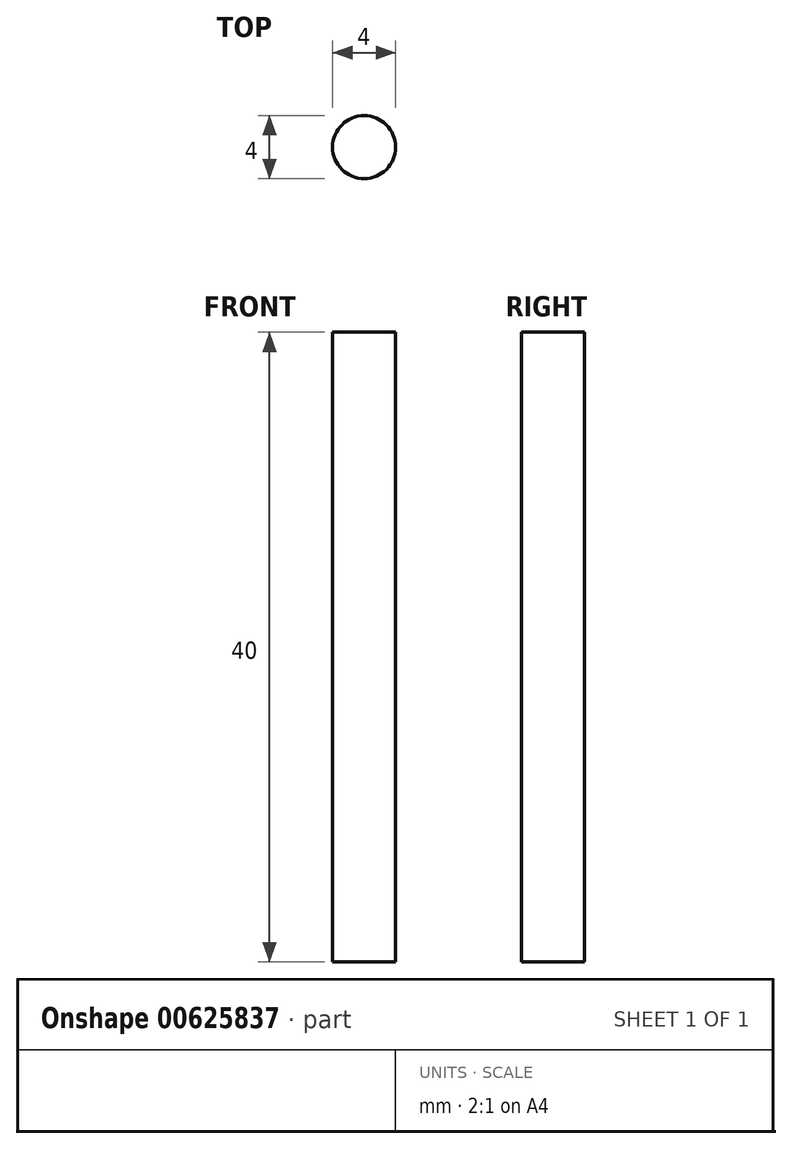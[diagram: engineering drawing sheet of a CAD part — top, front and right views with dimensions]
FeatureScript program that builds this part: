
annotation { "Feature Type Name" : "Feature", "Feature Type Description" : "" }
export const myFeature = defineFeature(function(context is Context, id is Id, definition is map)
    precondition{}
    {
        {
            var Q0;
            Q0=qCreatedBy(makeId("Top.planeOp"),FACE);
            var sketch = newSketch(context, id + "F0", { "sketchPlane" : qUnion([Q0])});
            skCircle(sketch, "E0", {"center": v(0, 0) * mm, "radius": 2 * mm});
            skSolve(sketch);
        }
        {
            var Q0;
            Q0=makeQuery(id+"F0.imprint","IMPRINT",FACE,{"disambiguationData":[TD([[makeQuery(id+"F0.imprint","IMPRINT",EDGE,{"derivedFrom":sQuery(id+"F0.wireOp",EDGE,"E0")}),1.0]])]});
            extrude(context, id + "F1", {"entities" : qUnion([Q0]), "depth" : 40 * mm, "offsetDistance" : 25 * mm});
        }
    });
